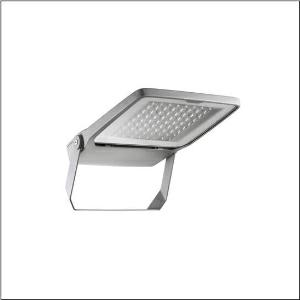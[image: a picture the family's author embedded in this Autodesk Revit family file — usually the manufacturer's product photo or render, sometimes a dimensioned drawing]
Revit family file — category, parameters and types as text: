
# Revit family: floodlight_fl_20_mini___rs17_5xa7672b2b1ac_377e
name_source: partatom
category: Lighting Fixtures
units: mm (PartAtom-declared; Revit-internal decimal feet)

## family parameters
Cut with Voids When Loaded = No
Host = Face
Light Source = No
Part Type = Normal
Room Calculation Point = No
Round Connector Dimension = Use Diameter
Shared = No

## types (1)
- --- (1 x LED 4000K / CRI = 70 (unbekannt), 6810 lm, 4000K)
    Apparent Load = 51 VA
    CIE Flux Codes = 79 92 99 100 100
    Color Rendering = 70
    Color Temperature = 4000K
    Default Elevation = 1800 mm
    Description = Floodlight FL 20 mini, floodlight, primary light control with lens, of plastic, primary optical cover: protective disc, of toughened safety glass, transparent, light distribution: RS17, light emission: direct distribution, primary light characteristic: rotationally symmetric, installation type: surface-mounted, LED, High Power LED, rated luminous flux: 6.810lm, luminous efficacy: 134lm/W, light colour: 740, colour temperature: 4000K, control gear: ECG Plus, control: flexible luminous flux parameterisation, time-dependent luminous flux control, digital communication interface, power reduction, overheat protection, electronic power reduction, with terminal, 5-pole, max. 2.5mm², mains connection: 220..240V, AC, 50/60Hz, rated input power: 51W, LED unit, of diecast aluminium, powder-coated, Siteco® metallic grey (DB 702S), corrosivity category C5 mid according to DIN EN ISO 12944, incl. 1x M20 cable gland for cable Ø 6.5..12mm, length: 446mm, width: 355mm, height: 62mm, housing frame, of diecast aluminium, powder-coated, Siteco® metallic grey (DB 702S), mounting bracket, of steel, powder-coated, Siteco® metallic grey (DB 702S), DALI, protection rating (complete): IP66, insulation class (complete): insulation class II (safety insulation), certification: CE, ENEC, VDE, protection symbol: D, permissible operating ambient temperature: -40..+40°C, permissible operating ambient temperature for outdoor applications: -40..+50°C, standard: DIN EN 12944, packaging unit: 1 piece

Light Distribution: RS17
    Height = 62 mm
    Lamp = 1 x LED 4000K / CRI >= 70 (unbekannt)
    Lamp Light Flux = 6810 lm
    Lamp count = 1
    Length = 467 mm
    Luminous efficacy = 134 lm/W
    Manufacturer = Siteco
    ModVariant = No
    Model = 5XA7672B2B1AC
    Mounting Place = Wall
    Mounting Type = Surface mounted
    Number of Poles = 1
    OnlyDefault = Yes
    Power Factor = 1
    Product Name = Floodlight FL 20 mini | RS17
    Product group = floodlight | wall mounted
    ProductGroupID = 2001
    Protection Class = Protection class II
    Protection Degree = IP 66
    RLX_Detail_Level = 1
    RLX_Emergency_Light_Flux = 0 lm
    RLX_Emergency_Type = 0
    RLX_Emergency_Type_DB = No
    RlxData = <blob elided: 68837 chars, md5=08681100>
    Socket = socket
    Standby Power = 0 W
    System Light Flux = 6810 lm
    System Power = 51 W
    Type Comments = factory setting: luminous flux: 100 % | dim-lin: 254 | 520 mA
    Type Image = l_1005948.jpg
    URL = http://relux.com
    VarID = @adj_163085
    Voltage = 0 V
    Weight = 0.00 kg
    Width = 335 mm

## geometry (parser evidence)
native form markers: Blend x4, Sweep x11
no freeform markers — native parametric forms only
